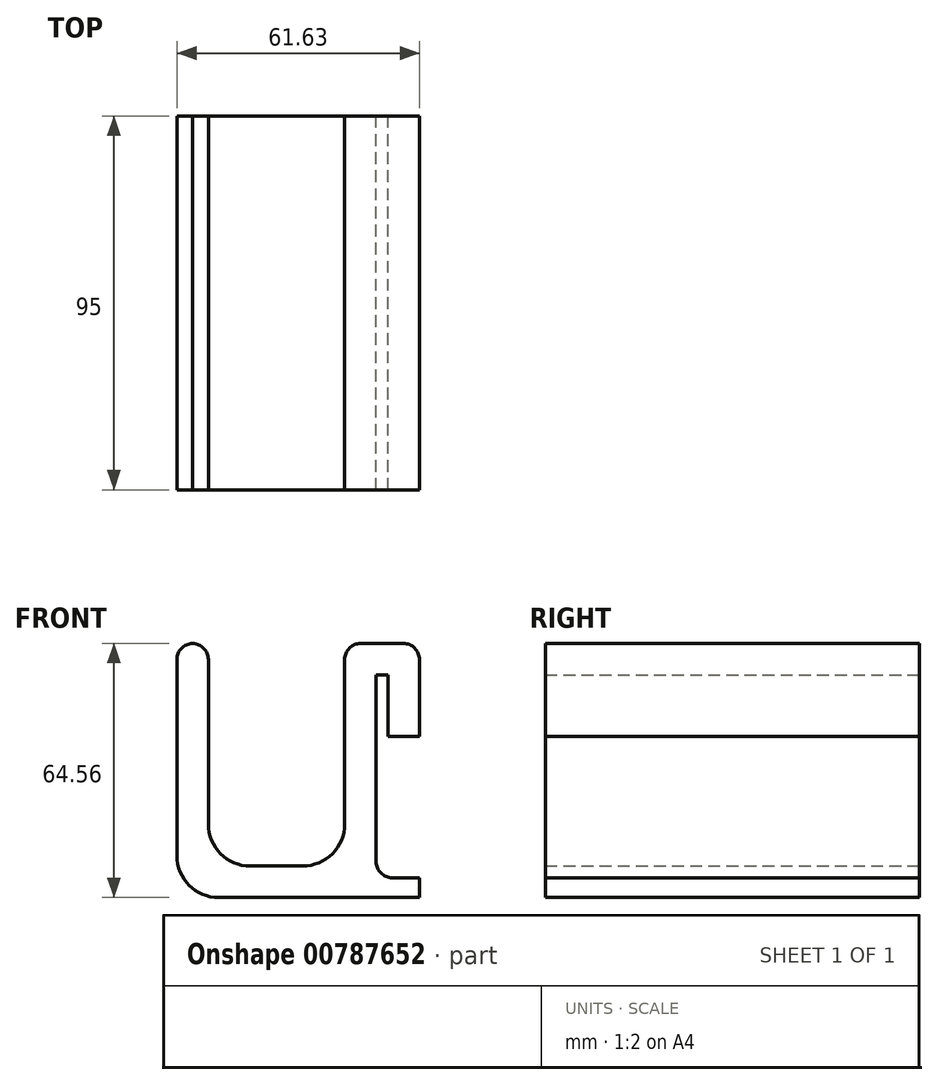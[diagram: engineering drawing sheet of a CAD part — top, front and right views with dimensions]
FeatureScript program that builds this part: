
annotation { "Feature Type Name" : "Feature", "Feature Type Description" : "" }
export const myFeature = defineFeature(function(context is Context, id is Id, definition is map)
    precondition{}
    {
        {
            var Q0;
            Q0=qCreatedBy(makeId("Front.planeOp"),FACE);
            var sketch = newSketch(context, id + "F0", { "sketchPlane" : qUnion([Q0])});
            skLineSegment(sketch, "E0", {"start": v(0, 0) * mm, "end": v(0, 56.56) * mm});
            skLineSegment(sketch, "E1", {"start": v(0, 56.56) * mm, "end": v(19, 56.56) * mm});
            skLineSegment(sketch, "E2", {"start": v(19, 56.56) * mm, "end": v(19, 32.93) * mm});
            skLineSegment(sketch, "E3", {"start": v(19, 32.93) * mm, "end": v(11, 32.93) * mm});
            skLineSegment(sketch, "E4", {"start": v(11, 32.93) * mm, "end": v(11, 48.56) * mm});
            skLineSegment(sketch, "E5", {"start": v(11, 48.56) * mm, "end": v(8, 48.56) * mm});
            skLineSegment(sketch, "E6", {"start": v(8, 48.56) * mm, "end": v(8, -3) * mm});
            skLineSegment(sketch, "E7", {"start": v(0, 0) * mm, "end": v(-34.63, 0) * mm});
            skLineSegment(sketch, "E8", {"start": v(-34.63, 0) * mm, "end": v(-34.63, 56.56) * mm});
            skLineSegment(sketch, "E9", {"start": v(-34.63, 56.56) * mm, "end": v(-42.63, 56.56) * mm});
            skLineSegment(sketch, "E10", {"start": v(-42.63, 56.56) * mm, "end": v(-42.63, -8) * mm});
            skLineSegment(sketch, "E11", {"start": v(-42.63, -8) * mm, "end": v(8, -8) * mm});
            skLineSegment(sketch, "E12", {"start": v(8, -8) * mm, "end": v(19, -8) * mm});
            skLineSegment(sketch, "E13", {"start": v(19, -8) * mm, "end": v(19, -3) * mm});
            skLineSegment(sketch, "E14", {"start": v(19, -3) * mm, "end": v(8, -3) * mm});
            skSolve(sketch);
        }
        {
            var Q0;
            Q0=makeQuery(id+"F0.imprint","IMPRINT",FACE,{"disambiguationData":[TD([[makeQuery(id+"F0.imprint","IMPRINT",EDGE,{"derivedFrom":sQuery(id+"F0.wireOp",EDGE,"E0")}),-1.0]])]});
            extrude(context, id + "F1", {"entities" : qUnion([Q0]), "depth" : 95 * mm, "offsetDistance" : 25 * mm});
        }
        {
            var Q0;
            Q0=makeQuery(id+"F1.opExtrude","SWEPT_EDGE",EDGE,{"disambiguationData":[OSD([sQuery(id+"F0.wireOp",EDGE,"E9"),sQuery(id+"F0.wireOp",EDGE,"E10")])]});
            var Q1;
            Q1=makeQuery(id+"F1.opExtrude","SWEPT_EDGE",EDGE,{"disambiguationData":[OSD([sQuery(id+"F0.wireOp",EDGE,"E8"),sQuery(id+"F0.wireOp",EDGE,"E9")])]});
            var Q2;
            Q2=makeQuery(id+"F1.opExtrude","SWEPT_EDGE",EDGE,{"disambiguationData":[OSD([sQuery(id+"F0.wireOp",EDGE,"E0"),sQuery(id+"F0.wireOp",EDGE,"E1")])]});
            var Q3;
            Q3=makeQuery(id+"F1.opExtrude","SWEPT_EDGE",EDGE,{"disambiguationData":[OSD([sQuery(id+"F0.wireOp",EDGE,"E1"),sQuery(id+"F0.wireOp",EDGE,"E2")])]});
            var Q4;
            Q4=makeQuery(id+"F1.opExtrude","SWEPT_EDGE",EDGE,{"disambiguationData":[OSD([sQuery(id+"F0.wireOp",EDGE,"E6"),sQuery(id+"F0.wireOp",EDGE,"E14")])]});
            fillet(context, id + "F2", {"entities" : qUnion([Q0, Q1, Q2, Q3, Q4]), "radius" : 4.1 * mm, "tangentPropagation" : true, "allowEdgeOverflow" : false});
        }
        {
            var Q0;
            Q0=makeQuery(id+"F1.opExtrude","SWEPT_EDGE",EDGE,{"disambiguationData":[OSD([sQuery(id+"F0.wireOp",EDGE,"E7"),sQuery(id+"F0.wireOp",EDGE,"E8")])]});
            var Q1;
            Q1=makeQuery(id+"F1.opExtrude","SWEPT_EDGE",EDGE,{"disambiguationData":[OSD([sQuery(id+"F0.wireOp",EDGE,"E0"),sQuery(id+"F0.wireOp",EDGE,"E7")])]});
            var Q2;
            Q2=makeQuery(id+"F1.opExtrude","SWEPT_EDGE",EDGE,{"disambiguationData":[OSD([sQuery(id+"F0.wireOp",EDGE,"E10"),sQuery(id+"F0.wireOp",EDGE,"E11")])]});
            fillet(context, id + "F3", {"entities" : qUnion([Q0, Q1, Q2]), "radius" : 10.62 * mm, "tangentPropagation" : true, "allowEdgeOverflow" : false});
        }
    });
